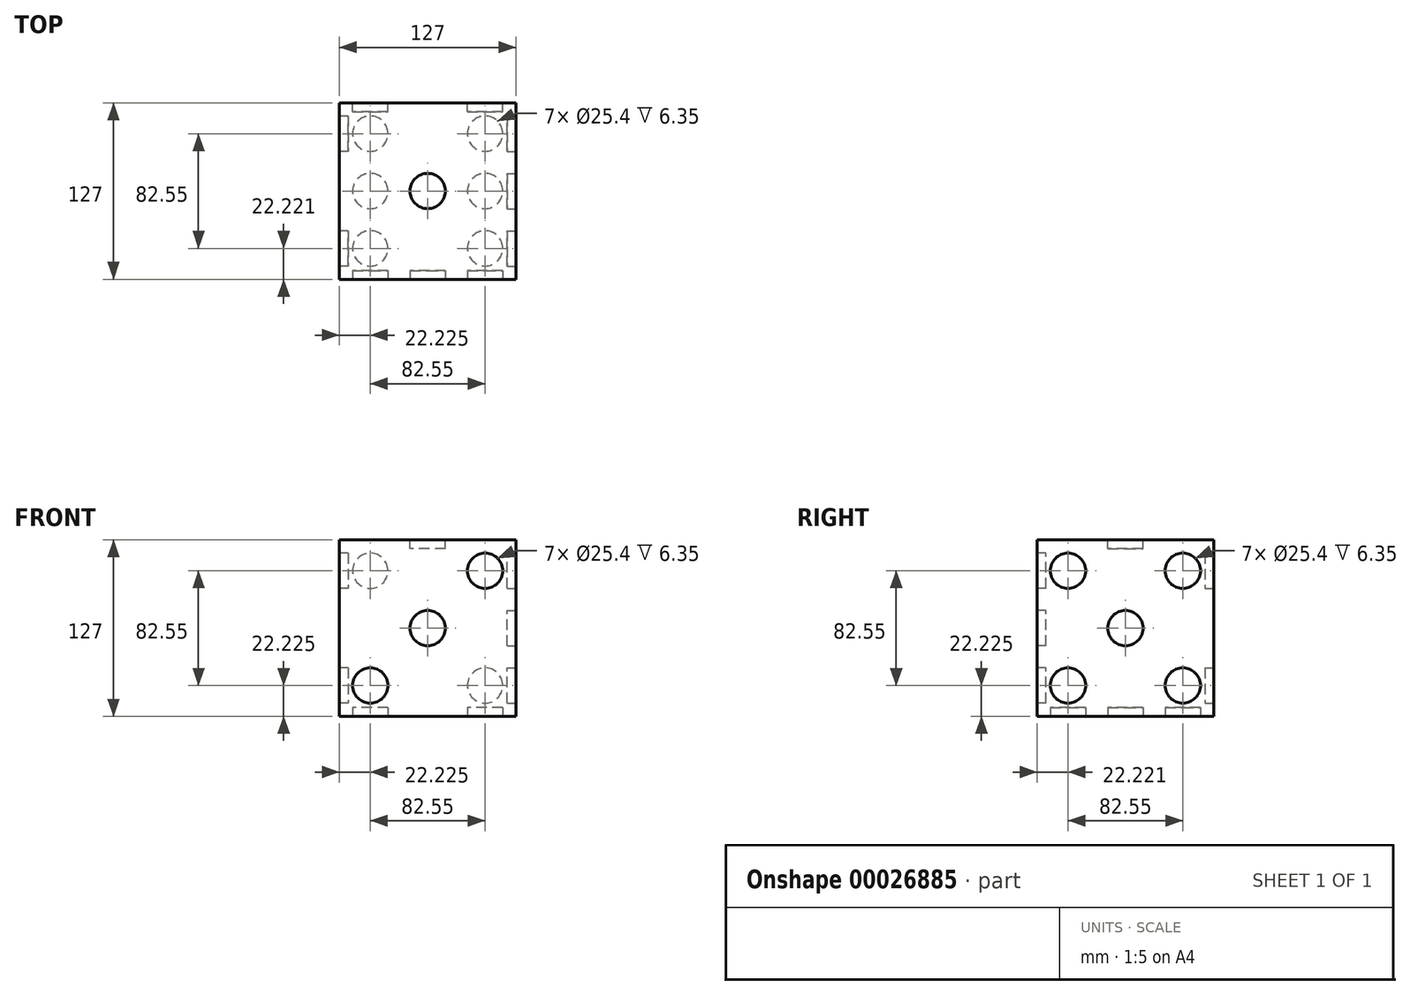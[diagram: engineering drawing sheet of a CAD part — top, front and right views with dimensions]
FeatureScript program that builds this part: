
annotation { "Feature Type Name" : "Feature", "Feature Type Description" : "" }
export const myFeature = defineFeature(function(context is Context, id is Id, definition is map)
    precondition{}
    {
        {
            var Q0;
            Q0=qCreatedBy(makeId("Top.planeOp"),FACE);
            var sketch = newSketch(context, id + "F0", { "sketchPlane" : qUnion([Q0])});
            skLineSegment(sketch, "E0.bottom", {"start": v(-1041.52, -38.17) * mm, "end": v(-914.52, -38.17) * mm});
            skLineSegment(sketch, "E0.top", {"start": v(-1041.52, -165.17) * mm, "end": v(-914.52, -165.17) * mm});
            skLineSegment(sketch, "E0.left", {"start": v(-1041.52, -38.17) * mm, "end": v(-1041.52, -165.17) * mm});
            skLineSegment(sketch, "E0.right", {"start": v(-914.52, -38.17) * mm, "end": v(-914.52, -165.17) * mm});
            skSolve(sketch);
        }
        {
            var Q0;
            Q0=makeQuery(id+"F0.imprint","IMPRINT",FACE,{"disambiguationData":[TD([[makeQuery(id+"F0.imprint","IMPRINT",EDGE,{"derivedFrom":sQuery(id+"F0.wireOp",EDGE,"E0.bottom")}),-1.0]])]});
            extrude(context, id + "F1", {"entities" : qUnion([Q0]), "depth" : 127 * mm});
        }
        {
            var Q0;
            Q0=makeQuery(id+"F1.opExtrude","CAP_FACE",FACE,{"disambiguationData":[OSD([sQuery(id+"F0.wireOp",EDGE,"E0.bottom"),sQuery(id+"F0.wireOp",EDGE,"E0.top"),sQuery(id+"F0.wireOp",EDGE,"E0.left"),sQuery(id+"F0.wireOp",EDGE,"E0.right")])],"isStart":false});
            var sketch = newSketch(context, id + "F2", { "sketchPlane" : qUnion([Q0])});
            skCircle(sketch, "E1", {"center": v(-978.02, -101.67) * mm, "radius": 12.7 * mm});
            skSolve(sketch);
        }
        {
            var Q0;
            Q0 = qSketchRegion(id + "F2", true);
            extrude(context, id + "F3", {"entities" : qUnion([Q0]), "operationType" : NewBodyOperationType.REMOVE, "oppositeDirection" : true, "depth" : 6.35 * mm});
        }
        {
            var Q0;
            Q0=makeQuery(id+"F1.opExtrude","SWEPT_FACE",FACE,{"disambiguationData":[OSD([sQuery(id+"F0.wireOp",EDGE,"E0.top")])]});
            var sketch = newSketch(context, id + "F4", { "sketchPlane" : qUnion([Q0])});
            skCircle(sketch, "E2", {"center": v(-978.02, 63.5) * mm, "radius": 12.7 * mm});
            skCircle(sketch, "E3", {"center": v(-936.75, 104.78) * mm, "radius": 12.7 * mm});
            skCircle(sketch, "E4", {"center": v(-1019.3, 22.22) * mm, "radius": 12.7 * mm});
            skSolve(sketch);
        }
        {
            var Q0;
            Q0 = qSketchRegion(id + "F4", true);
            extrude(context, id + "F5", {"entities" : qUnion([Q0]), "operationType" : NewBodyOperationType.REMOVE, "oppositeDirection" : true, "depth" : 6.35 * mm});
        }
        {
            var Q0;
            Q0=makeQuery(id+"F1.opExtrude","SWEPT_FACE",FACE,{"disambiguationData":[OSD([sQuery(id+"F0.wireOp",EDGE,"E0.left")])]});
            var sketch = newSketch(context, id + "F6", { "sketchPlane" : qUnion([Q0])});
            skCircle(sketch, "E5", {"center": v(60.4, 22.22) * mm, "radius": 12.7 * mm});
            skCircle(sketch, "E6", {"center": v(142.95, 104.78) * mm, "radius": 12.7 * mm});
            skSolve(sketch);
        }
        {
            var Q0;
            Q0=makeQuery(id+"F6.imprint","IMPRINT",FACE,{"disambiguationData":[TD([[makeQuery(id+"F6.imprint","IMPRINT",EDGE,{"derivedFrom":sQuery(id+"F6.wireOp",EDGE,"E5")}),1.0]])]});
            var Q1;
            Q1=makeQuery(id+"F6.imprint","IMPRINT",FACE,{"disambiguationData":[TD([[makeQuery(id+"F6.imprint","IMPRINT",EDGE,{"derivedFrom":sQuery(id+"F6.wireOp",EDGE,"E6")}),1.0]])]});
            extrude(context, id + "F7", {"entities" : qUnion([Q0, Q1]), "operationType" : NewBodyOperationType.REMOVE, "oppositeDirection" : true, "depth" : 6.35 * mm});
        }
        {
            var Q0;
            Q0=makeQuery(id+"F1.opExtrude","SWEPT_FACE",FACE,{"disambiguationData":[OSD([sQuery(id+"F0.wireOp",EDGE,"E0.bottom")])]});
            var sketch = newSketch(context, id + "F8", { "sketchPlane" : qUnion([Q0])});
            skCircle(sketch, "E7", {"center": v(936.75, 104.78) * mm, "radius": 12.7 * mm});
            skCircle(sketch, "E8", {"center": v(1019.3, 104.78) * mm, "radius": 12.7 * mm});
            skCircle(sketch, "E9", {"center": v(1019.3, 22.22) * mm, "radius": 12.7 * mm});
            skCircle(sketch, "E10", {"center": v(936.75, 22.22) * mm, "radius": 12.7 * mm});
            skSolve(sketch);
        }
        {
            var Q0;
            Q0=makeQuery(id+"F8.imprint","IMPRINT",FACE,{"disambiguationData":[TD([[makeQuery(id+"F8.imprint","IMPRINT",EDGE,{"derivedFrom":sQuery(id+"F8.wireOp",EDGE,"E7")}),1.0]])]});
            var Q1;
            Q1=makeQuery(id+"F8.imprint","IMPRINT",FACE,{"disambiguationData":[TD([[makeQuery(id+"F8.imprint","IMPRINT",EDGE,{"derivedFrom":sQuery(id+"F8.wireOp",EDGE,"E8")}),1.0]])]});
            var Q2;
            Q2=makeQuery(id+"F8.imprint","IMPRINT",FACE,{"disambiguationData":[TD([[makeQuery(id+"F8.imprint","IMPRINT",EDGE,{"derivedFrom":sQuery(id+"F8.wireOp",EDGE,"E9")}),1.0]])]});
            var Q3;
            Q3=makeQuery(id+"F8.imprint","IMPRINT",FACE,{"disambiguationData":[TD([[makeQuery(id+"F8.imprint","IMPRINT",EDGE,{"derivedFrom":sQuery(id+"F8.wireOp",EDGE,"E10")}),1.0]])]});
            extrude(context, id + "F9", {"entities" : qUnion([Q0, Q1, Q2, Q3]), "operationType" : NewBodyOperationType.REMOVE, "oppositeDirection" : true, "depth" : 6.35 * mm});
        }
        {
            var Q0;
            Q0=makeQuery(id+"F1.opExtrude","SWEPT_FACE",FACE,{"disambiguationData":[OSD([sQuery(id+"F0.wireOp",EDGE,"E0.right")])]});
            var sketch = newSketch(context, id + "F10", { "sketchPlane" : qUnion([Q0])});
            skCircle(sketch, "E11", {"center": v(-101.67, 63.5) * mm, "radius": 12.7 * mm});
            skCircle(sketch, "E12", {"center": v(-60.4, 104.78) * mm, "radius": 12.7 * mm});
            skCircle(sketch, "E13", {"center": v(-142.95, 104.78) * mm, "radius": 12.7 * mm});
            skCircle(sketch, "E14", {"center": v(-142.95, 22.22) * mm, "radius": 12.7 * mm});
            skCircle(sketch, "E15", {"center": v(-60.4, 22.23) * mm, "radius": 12.7 * mm});
            skSolve(sketch);
        }
        {
            var Q0;
            Q0 = qSketchRegion(id + "F10", true);
            extrude(context, id + "F11", {"entities" : qUnion([Q0]), "operationType" : NewBodyOperationType.REMOVE, "oppositeDirection" : true, "depth" : 6.35 * mm});
        }
        {
            var Q0;
            Q0=makeQuery(id+"F0.imprint","IMPRINT",FACE,{"disambiguationData":[TD([[makeQuery(id+"F0.imprint","IMPRINT",EDGE,{"derivedFrom":sQuery(id+"F0.wireOp",EDGE,"E0.bottom")}),-1.0]])]});
            var sketch = newSketch(context, id + "F12", { "sketchPlane" : qUnion([Q0])});
            skCircle(sketch, "E16", {"center": v(-936.75, -142.95) * mm, "radius": 12.7 * mm});
            skCircle(sketch, "E17", {"center": v(-1019.3, -142.95) * mm, "radius": 12.7 * mm});
            skCircle(sketch, "E18", {"center": v(-1019.3, -60.4) * mm, "radius": 12.7 * mm});
            skCircle(sketch, "E19", {"center": v(-936.75, -101.67) * mm, "radius": 12.7 * mm});
            skCircle(sketch, "E20", {"center": v(-1019.3, -101.67) * mm, "radius": 12.7 * mm});
            skCircle(sketch, "E21", {"center": v(-936.75, -60.4) * mm, "radius": 12.7 * mm});
            skSolve(sketch);
        }
        {
            var Q0;
            Q0=makeQuery(id+"F12.imprint","IMPRINT",FACE,{"disambiguationData":[TD([[makeQuery(id+"F12.imprint","IMPRINT",EDGE,{"derivedFrom":sQuery(id+"F12.wireOp",EDGE,"E16")}),1.0]])]});
            var Q1;
            Q1=makeQuery(id+"F12.imprint","IMPRINT",FACE,{"disambiguationData":[TD([[makeQuery(id+"F12.imprint","IMPRINT",EDGE,{"derivedFrom":sQuery(id+"F12.wireOp",EDGE,"E17")}),1.0]])]});
            var Q2;
            Q2=makeQuery(id+"F12.imprint","IMPRINT",FACE,{"disambiguationData":[TD([[makeQuery(id+"F12.imprint","IMPRINT",EDGE,{"derivedFrom":sQuery(id+"F12.wireOp",EDGE,"E18")}),1.0]])]});
            var Q3;
            Q3=makeQuery(id+"F12.imprint","IMPRINT",FACE,{"disambiguationData":[TD([[makeQuery(id+"F12.imprint","IMPRINT",EDGE,{"derivedFrom":sQuery(id+"F12.wireOp",EDGE,"E19")}),1.0]])]});
            var Q4;
            Q4=makeQuery(id+"F12.imprint","IMPRINT",FACE,{"disambiguationData":[TD([[makeQuery(id+"F12.imprint","IMPRINT",EDGE,{"derivedFrom":sQuery(id+"F12.wireOp",EDGE,"E20")}),1.0]])]});
            var Q5;
            Q5=makeQuery(id+"F12.imprint","IMPRINT",FACE,{"disambiguationData":[TD([[makeQuery(id+"F12.imprint","IMPRINT",EDGE,{"derivedFrom":sQuery(id+"F12.wireOp",EDGE,"E21")}),1.0]])]});
            extrude(context, id + "F13", {"entities" : qUnion([Q0, Q1, Q2, Q3, Q4, Q5]), "operationType" : NewBodyOperationType.REMOVE, "depth" : 6.35 * mm});
        }
    });
